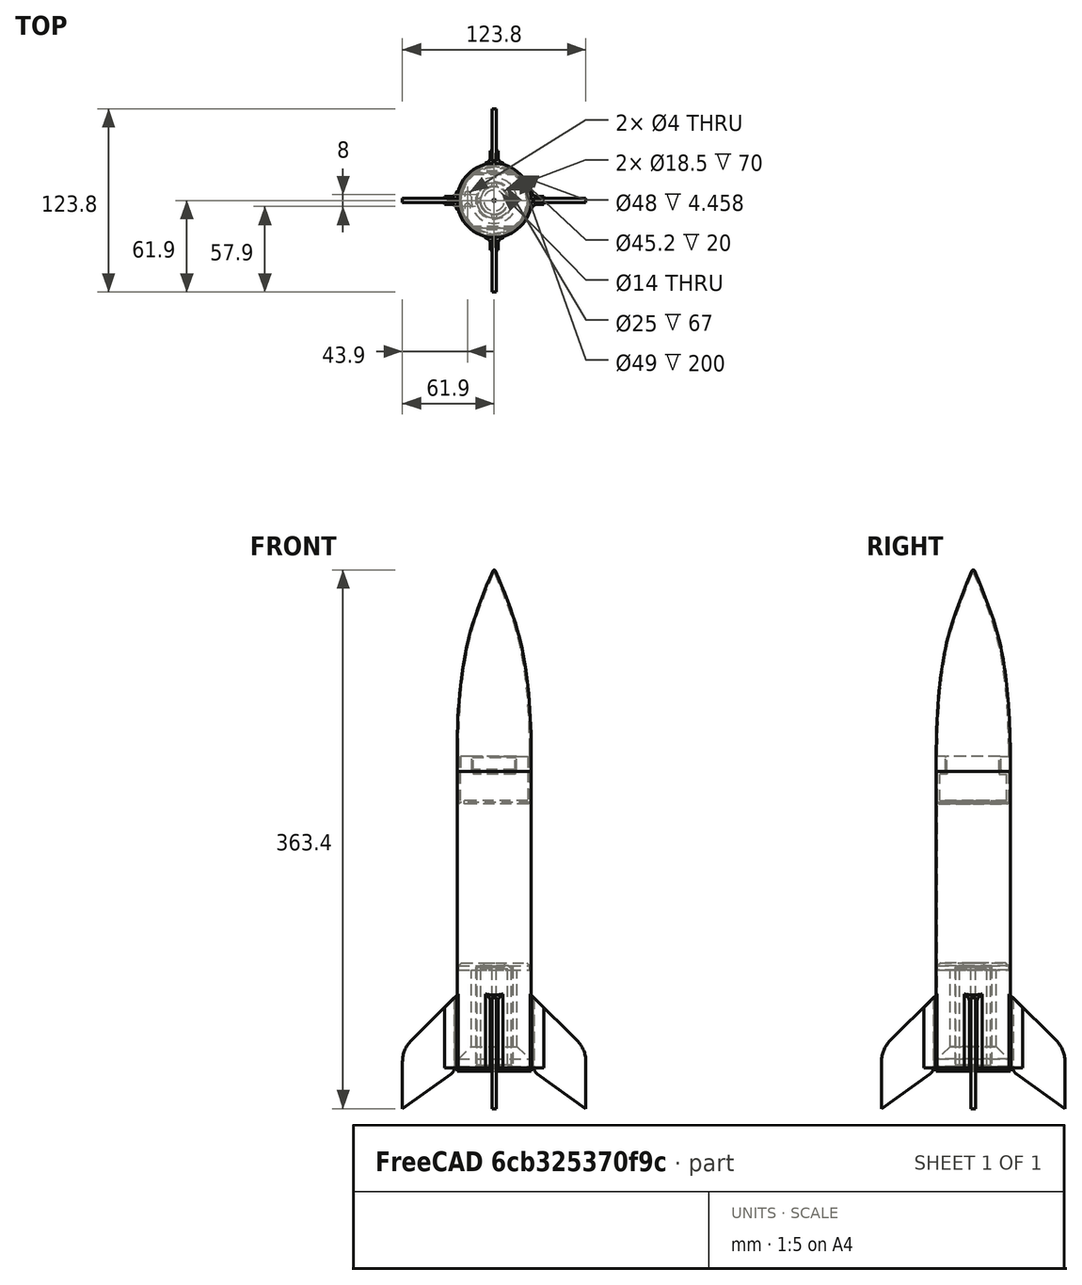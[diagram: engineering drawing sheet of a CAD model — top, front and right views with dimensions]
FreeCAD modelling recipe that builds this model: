
FCSTD DOCUMENT  (FreeCAD 0.19R)
Label: LaMule_support_moteur_V1
License: All rights reserved
LicenseURL: http://en.wikipedia.org/wiki/All_rights_reserved
objects: Sketcher::SketchObject×26, PartDesign::Pad×16, PartDesign::Body×14, PartDesign::Fillet×12, PartDesign::Pocket×8, PartDesign::Chamfer×7, Mesh::Feature×3, PartDesign::Revolution×2, App::LinkGroup×2, PartDesign::Thickness×1, TechDraw::DrawSVGTemplate×1, TechDraw::DrawViewPart×1, TechDraw::DrawPage×1
note: 132 computed .brp shape members not serialized (recipe doc carries the construction recipe); baked Part::Feature solids carry a one-line shape summary decoded from their .brp

FEATURE [Sketcher::SketchObject] Sketch
  FullyConstrained = true
  MapMode = 5
  Placement = pos=(0,0,0) rot=(1,0,0;1.5708rad)
  Support = -> [XZ_Plane]
  sketch-geometry (12):
    g0: LineSegment StartX=24 StartY=0 StartZ=0 EndX=7 EndY=0 EndZ=0
    g1: LineSegment StartX=7 StartY=0 StartZ=0 EndX=7 EndY=3 EndZ=0
    g2: LineSegment StartX=7 StartY=3 StartZ=0 EndX=12.5 EndY=3 EndZ=0
    g3: LineSegment StartX=12.5 StartY=3 StartZ=0 EndX=12.5 EndY=73 EndZ=0
    g4: LineSegment StartX=12.5 StartY=73 StartZ=0 EndX=25 EndY=73 EndZ=0
    g5: LineSegment StartX=25 StartY=73 StartZ=0 EndX=25 EndY=71 EndZ=0
    g6: LineSegment StartX=25 StartY=71 StartZ=0 EndX=24 EndY=70 EndZ=0
    g7: LineSegment StartX=24 StartY=70 StartZ=0 EndX=24 EndY=65 EndZ=0
    g8: LineSegment StartX=24 StartY=65 StartZ=0 EndX=15.5 EndY=56.5 EndZ=0
    g9: LineSegment StartX=15.5 StartY=56.5 StartZ=0 EndX=15.5 EndY=5 EndZ=0
    g10: LineSegment StartX=15.5 StartY=5 StartZ=0 EndX=24 EndY=5 EndZ=0
    g11: LineSegment StartX=24 StartY=5 StartZ=0 EndX=24 EndY=0 EndZ=0
  constraints (36):
    c: PointOnObject(g0,g-1)
    c: PointOnObject(g0,g-1)
    c: Coincident(g0,g1)
    c: Vertical(g1)
    c: Coincident(g1,g2)
    c: Horizontal(g2)
    c: Coincident(g2,g3)
    c: Vertical(g3)
    c: Coincident(g3,g4)
    c: Horizontal(g4)
    c: Coincident(g4,g5)
    c: Coincident(g5,g6)
    c: Coincident(g6,g7)
    c: Vertical(g7)
    c: Coincident(g7,g8)
    c: Coincident(g8,g9)
    c: Vertical(g9)
    c: Coincident(g9,g10)
    c: Horizontal(g10)
    c: Coincident(g10,g11)
    c: Coincident(g11,g0)
    c: DistanceX(g-2,g2) = 12.5
    c: DistanceY(g3,g3) = 70
    c: DistanceY(g1,g1) = 3
    c: DistanceX(g-2,g4) = 25
    c: Vertical(g5)
    c: DistanceY(g5,g5) = 2
    c: DistanceY(g7,g7) = 5
    c: DistanceX(g-1,g0) = 24
    c: DistanceX(g-2,g7) = 24
    c: Distance(g9,g3) = 3
    c: DistanceY(g11,g11) = 5
    c: Angle(g9,g8) = 2.35619
    c: Angle(g7,g6) = 2.35619
    c: Vertical(g11)
    c: DistanceX(g-2,g0) = 7
FEATURE [PartDesign::Revolution] Revolution
  Angle = 360
  Axis = (0,2e-16,1)
  Base = (0,0,0)
  Placement = pos=(0,0,0) rot=(1,0,0;1.5708rad)
  Profile = -> Sketch
  ReferenceAxis = -> Sketch [V_Axis]
  Reversed = true
FEATURE [PartDesign::Chamfer] Chamfer
  Angle = 45
  Base = -> Revolution [Edge6]
  BaseFeature = -> Revolution
  ChamferType = 0
  FlipDirection = false
  Placement = pos=(0,0,0) rot=(1,0,0;1.5708rad)
  Size = 3
  Size2 = 1
  SupportTransform = false
FEATURE [PartDesign::Chamfer] Chamfer001
  Angle = 45
  Base = -> Chamfer [Edge12]
  BaseFeature = -> Chamfer
  ChamferType = 0
  FlipDirection = false
  Placement = pos=(0,0,0) rot=(1,0,0;1.5708rad)
  Size = 2
  Size2 = 1
  SupportTransform = false
FEATURE [PartDesign::Body] Body  label="support_moteur_V1"
  Group = -> [Sketch,Revolution,Chamfer,Chamfer001]
  Origin = -> Origin
  Placement = pos=(7e-15,0,71) rot=(0,1,0;3.14159rad)
  Tip = -> Chamfer001
FEATURE [Sketcher::SketchObject] Sketch001
  FullyConstrained = true
  MapMode = 5
  Support = -> [XY_Plane001]
  sketch-geometry (2):
    g0: Circle CenterX=0 CenterY=0 CenterZ=0 NormalX=0 NormalY=0 NormalZ=1 AngleXU=0 Radius=24.5
    g1: Circle CenterX=0 CenterY=0 CenterZ=0 NormalX=0 NormalY=0 NormalZ=1 AngleXU=0 Radius=25
  constraints (4):
    c: Radius(g0) = 24.5
    c: Radius(g1) = 25
    c: Coincident(g0,g-1)
    c: Coincident(g1,g0)
FEATURE [PartDesign::Pad] Pad
  Direction = (1,1,1)
  Length = 200
  Length2 = 100
  Profile = -> Sketch001
  Type = 0
FEATURE [PartDesign::Body] Body001  label="tube_V1"
  Group = -> [Sketch001,Pad]
  Origin = -> Origin001
  Tip = -> Pad
FEATURE [Sketcher::SketchObject] Sketch002
  FullyConstrained = true
  MapMode = 5
  Support = -> [XY_Plane002]
  sketch-geometry (12):
    g0: ArcOfCircle CenterX=0 CenterY=0 CenterZ=0 NormalX=0 NormalY=0 NormalZ=1 AngleXU=0 Radius=25 StartAngle=6.04082 EndAngle=6.52555
    g1: LineSegment StartX=24.2693 StartY=-6 StartZ=0 EndX=25.2982 EndY=-6 EndZ=0
    g2: LineSegment StartX=24.2693 StartY=6 StartZ=0 EndX=25.2982 EndY=6 EndZ=0
    g3: LineSegment StartX=25.8697 StartY=2.6 StartZ=0 EndX=33.4517 EndY=2.6 EndZ=0
    g4: LineSegment StartX=33.4517 StartY=2.6 StartZ=0 EndX=33.4517 EndY=1.6 EndZ=0
    g5: LineSegment StartX=33.4517 StartY=1.6 StartZ=0 EndX=26.4517 EndY=1.6 EndZ=0
    g6: LineSegment StartX=26.4517 StartY=1.6 StartZ=0 EndX=26.4517 EndY=-1.6 EndZ=0
    g7: LineSegment StartX=26.4517 StartY=-1.6 StartZ=0 EndX=33.4517 EndY=-1.6 EndZ=0
    g8: LineSegment StartX=33.4517 StartY=-1.6 StartZ=0 EndX=33.4517 EndY=-2.6 EndZ=0
    g9: LineSegment StartX=33.4517 StartY=-2.6 StartZ=0 EndX=25.8697 EndY=-2.6 EndZ=0
    g10: ArcOfCircle CenterX=0 CenterY=0 CenterZ=0 NormalX=0 NormalY=0 NormalZ=1 AngleXU=0 Radius=26 StartAngle=6.05032 EndAngle=6.18302
    g11: ArcOfCircle CenterX=0 CenterY=0 CenterZ=0 NormalX=0 NormalY=0 NormalZ=1 AngleXU=0 Radius=26 StartAngle=0.100167 EndAngle=0.232868
  constraints (33):
    c: Coincident(g0,g-1)
    c: Radius(g0) = 25
    c: Coincident(g0,g1)
    c: Coincident(g0,g2)
    c: Horizontal(g3)
    c: Coincident(g3,g4)
    c: Coincident(g4,g5)
    c: Horizontal(g5)
    c: Coincident(g5,g6)
    c: Coincident(g6,g7)
    c: Horizontal(g7)
    c: Coincident(g7,g8)
    c: Coincident(g8,g9)
    c: Horizontal(g9)
    c: Coincident(g10,g0)
    c: Coincident(g10,g1)
    c: Coincident(g10,g9)
    c: Coincident(g11,g0)
    c: Coincident(g11,g2)
    c: Coincident(g11,g3)
    c: Radius(g11) = 26
    c: Horizontal(g2)
    c: Horizontal(g1)
    c: Symmetric(g7,g4,g-1)
    c: Vertical(g8)
    c: Vertical(g6)
    c: Distance(g6,g5) = 3.2
    c: DistanceY(g4,g4) = 1
    c: Distance(g5,g0) = 26.5
    c: Symmetric(g3,g8,g-1)
    c: DistanceX(g5,g5) = 7
    c: Symmetric(g2,g1,g-1)
    c: DistanceY(g-1,g2) = 6
FEATURE [PartDesign::Pad] Pad001
  Direction = (1,1,1)
  Length = 50
  Length2 = 100
  Profile = -> Sketch002
  Type = 0
FEATURE [PartDesign::Fillet] Fillet
  Base = -> Pad001 [Edge20,Edge1]
  BaseFeature = -> Pad001
  Radius = 4
  SupportTransform = false
FEATURE [Sketcher::SketchObject] Sketch003
  ExternalGeometry = -> [Fillet]
  FullyConstrained = true
  MapMode = 5
  Placement = pos=(0,-2.6,0) rot=(1,0,0;1.5708rad)
  Support = -> [Fillet]
  sketch-geometry (3):
    g0: LineSegment StartX=33.4517 StartY=50 StartZ=0 EndX=33.4517 EndY=40.8177 EndZ=0
    g1: LineSegment StartX=33.4517 StartY=40.8177 StartZ=0 EndX=24.2693 EndY=50 EndZ=0
    g2: LineSegment StartX=24.2693 StartY=50 StartZ=0 EndX=33.4517 EndY=50 EndZ=0
  constraints (8):
    c: Coincident(g-4,g0)
    c: PointOnObject(g0,g-4)
    c: Coincident(g0,g1)
    c: PointOnObject(g1,g-3)
    c: Coincident(g1,g2)
    c: Coincident(g2,g0)
    c: Horizontal(g2)
    c: Angle(g1,g2) = 0.785398
FEATURE [PartDesign::Pocket] Pocket
  BaseFeature = -> Fillet
  Length = 23
  Length2 = 100
  Midplane = true
  Profile = -> Sketch003
  Type = 1
FEATURE [PartDesign::Body] Body002  label="support_aileron_V1"
  Group = -> [Sketch002,Pad001,Fillet,Sketch003,Pocket]
  Origin = -> Origin002
  Tip = -> Pocket
FEATURE [Sketcher::SketchObject] Sketch004
  FullyConstrained = true
  MapMode = 5
  Support = -> [XY_Plane003]
  sketch-geometry (12):
    g0: ArcOfCircle CenterX=0 CenterY=0 CenterZ=0 NormalX=0 NormalY=0 NormalZ=1 AngleXU=0 Radius=25 StartAngle=6.04082 EndAngle=6.52555
    g1: LineSegment StartX=24.2693 StartY=-6 StartZ=0 EndX=25.2982 EndY=-6 EndZ=0
    g2: LineSegment StartX=24.2693 StartY=6 StartZ=0 EndX=25.2982 EndY=6 EndZ=0
    g3: LineSegment StartX=25.8697 StartY=2.6 StartZ=0 EndX=33.4517 EndY=2.6 EndZ=0
    g4: LineSegment StartX=33.4517 StartY=2.6 StartZ=0 EndX=33.4517 EndY=1.6 EndZ=0
    g5: LineSegment StartX=33.4517 StartY=1.6 StartZ=0 EndX=26.4517 EndY=1.6 EndZ=0
    g6: LineSegment StartX=26.4517 StartY=1.6 StartZ=0 EndX=26.4517 EndY=-1.6 EndZ=0
    g7: LineSegment StartX=26.4517 StartY=-1.6 StartZ=0 EndX=33.4517 EndY=-1.6 EndZ=0
    g8: LineSegment StartX=33.4517 StartY=-1.6 StartZ=0 EndX=33.4517 EndY=-2.6 EndZ=0
    g9: LineSegment StartX=33.4517 StartY=-2.6 StartZ=0 EndX=25.8697 EndY=-2.6 EndZ=0
    g10: ArcOfCircle CenterX=0 CenterY=0 CenterZ=0 NormalX=0 NormalY=0 NormalZ=1 AngleXU=0 Radius=26 StartAngle=6.05032 EndAngle=6.18302
    g11: ArcOfCircle CenterX=0 CenterY=0 CenterZ=0 NormalX=0 NormalY=0 NormalZ=1 AngleXU=0 Radius=26 StartAngle=0.100167 EndAngle=0.232868
  constraints (33):
    c: Coincident(g0,g-1)
    c: Radius(g0) = 25
    c: Coincident(g0,g1)
    c: Coincident(g0,g2)
    c: Horizontal(g3)
    c: Coincident(g3,g4)
    c: Coincident(g4,g5)
    c: Horizontal(g5)
    c: Coincident(g5,g6)
    c: Coincident(g6,g7)
    c: Horizontal(g7)
    c: Coincident(g7,g8)
    c: Coincident(g8,g9)
    c: Horizontal(g9)
    c: Coincident(g10,g0)
    c: Coincident(g10,g1)
    c: Coincident(g10,g9)
    c: Coincident(g11,g0)
    c: Coincident(g11,g2)
    c: Coincident(g11,g3)
    c: Radius(g11) = 26
    c: Horizontal(g2)
    c: Horizontal(g1)
    c: Symmetric(g7,g4,g-1)
    c: Vertical(g8)
    c: Vertical(g6)
    c: Distance(g6,g5) = 3.2
    c: DistanceY(g4,g4) = 1
    c: Distance(g5,g0) = 26.5
    c: Symmetric(g3,g8,g-1)
    c: DistanceX(g5,g5) = 7
    c: Symmetric(g2,g1,g-1)
    c: DistanceY(g-1,g2) = 6
FEATURE [PartDesign::Pad] Pad002
  Direction = (1,1,1)
  Length = 50
  Length2 = 100
  Profile = -> Sketch004
  Type = 0
FEATURE [PartDesign::Fillet] Fillet001
  Base = -> Pad002 [Edge20,Edge1]
  BaseFeature = -> Pad002
  Radius = 4
  SupportTransform = false
FEATURE [Sketcher::SketchObject] Sketch005
  ExternalGeometry = -> [Fillet001]
  FullyConstrained = true
  MapMode = 5
  Placement = pos=(0,-2.6,0) rot=(1,0,0;1.5708rad)
  Support = -> [Fillet001]
  sketch-geometry (3):
    g0: LineSegment StartX=33.4517 StartY=50 StartZ=0 EndX=33.4517 EndY=40.8177 EndZ=0
    g1: LineSegment StartX=33.4517 StartY=40.8177 StartZ=0 EndX=24.2693 EndY=50 EndZ=0
    g2: LineSegment StartX=24.2693 StartY=50 StartZ=0 EndX=33.4517 EndY=50 EndZ=0
  constraints (8):
    c: Coincident(g-4,g0)
    c: PointOnObject(g0,g-4)
    c: Coincident(g0,g1)
    c: PointOnObject(g1,g-3)
    c: Coincident(g1,g2)
    c: Coincident(g2,g0)
    c: Horizontal(g2)
    c: Angle(g1,g2) = 0.785398
FEATURE [PartDesign::Pocket] Pocket001
  BaseFeature = -> Fillet001
  Length = 23
  Length2 = 100
  Midplane = true
  Profile = -> Sketch005
  Type = 1
FEATURE [PartDesign::Body] Body003  label="support_aileron_V002"
  Group = -> [Sketch004,Pad002,Fillet001,Sketch005,Pocket001]
  Origin = -> Origin003
  Placement = pos=(0,0,0) rot=(0,0,1;1.5708rad)
  Tip = -> Pocket001
FEATURE [Sketcher::SketchObject] Sketch006
  FullyConstrained = true
  MapMode = 5
  Support = -> [XY_Plane004]
  sketch-geometry (12):
    g0: ArcOfCircle CenterX=0 CenterY=0 CenterZ=0 NormalX=0 NormalY=0 NormalZ=1 AngleXU=0 Radius=25 StartAngle=6.04082 EndAngle=6.52555
    g1: LineSegment StartX=24.2693 StartY=-6 StartZ=0 EndX=25.2982 EndY=-6 EndZ=0
    g2: LineSegment StartX=24.2693 StartY=6 StartZ=0 EndX=25.2982 EndY=6 EndZ=0
    g3: LineSegment StartX=25.8697 StartY=2.6 StartZ=0 EndX=33.4517 EndY=2.6 EndZ=0
    g4: LineSegment StartX=33.4517 StartY=2.6 StartZ=0 EndX=33.4517 EndY=1.6 EndZ=0
    g5: LineSegment StartX=33.4517 StartY=1.6 StartZ=0 EndX=26.4517 EndY=1.6 EndZ=0
    g6: LineSegment StartX=26.4517 StartY=1.6 StartZ=0 EndX=26.4517 EndY=-1.6 EndZ=0
    g7: LineSegment StartX=26.4517 StartY=-1.6 StartZ=0 EndX=33.4517 EndY=-1.6 EndZ=0
    g8: LineSegment StartX=33.4517 StartY=-1.6 StartZ=0 EndX=33.4517 EndY=-2.6 EndZ=0
    g9: LineSegment StartX=33.4517 StartY=-2.6 StartZ=0 EndX=25.8697 EndY=-2.6 EndZ=0
    g10: ArcOfCircle CenterX=0 CenterY=0 CenterZ=0 NormalX=0 NormalY=0 NormalZ=1 AngleXU=0 Radius=26 StartAngle=6.05032 EndAngle=6.18302
    g11: ArcOfCircle CenterX=0 CenterY=0 CenterZ=0 NormalX=0 NormalY=0 NormalZ=1 AngleXU=0 Radius=26 StartAngle=0.100167 EndAngle=0.232868
  constraints (33):
    c: Coincident(g0,g-1)
    c: Radius(g0) = 25
    c: Coincident(g0,g1)
    c: Coincident(g0,g2)
    c: Horizontal(g3)
    c: Coincident(g3,g4)
    c: Coincident(g4,g5)
    c: Horizontal(g5)
    c: Coincident(g5,g6)
    c: Coincident(g6,g7)
    c: Horizontal(g7)
    c: Coincident(g7,g8)
    c: Coincident(g8,g9)
    c: Horizontal(g9)
    c: Coincident(g10,g0)
    c: Coincident(g10,g1)
    c: Coincident(g10,g9)
    c: Coincident(g11,g0)
    c: Coincident(g11,g2)
    c: Coincident(g11,g3)
    c: Radius(g11) = 26
    c: Horizontal(g2)
    c: Horizontal(g1)
    c: Symmetric(g7,g4,g-1)
    c: Vertical(g8)
    c: Vertical(g6)
    c: Distance(g6,g5) = 3.2
    c: DistanceY(g4,g4) = 1
    c: Distance(g5,g0) = 26.5
    c: Symmetric(g3,g8,g-1)
    c: DistanceX(g5,g5) = 7
    c: Symmetric(g2,g1,g-1)
    c: DistanceY(g-1,g2) = 6
FEATURE [PartDesign::Pad] Pad003
  Direction = (1,1,1)
  Length = 50
  Length2 = 100
  Profile = -> Sketch006
  Type = 0
FEATURE [PartDesign::Fillet] Fillet002
  Base = -> Pad003 [Edge20,Edge1]
  BaseFeature = -> Pad003
  Radius = 4
  SupportTransform = false
FEATURE [Sketcher::SketchObject] Sketch007
  ExternalGeometry = -> [Fillet002]
  FullyConstrained = true
  MapMode = 5
  Placement = pos=(0,-2.6,0) rot=(1,0,0;1.5708rad)
  Support = -> [Fillet002]
  sketch-geometry (3):
    g0: LineSegment StartX=33.4517 StartY=50 StartZ=0 EndX=33.4517 EndY=40.8177 EndZ=0
    g1: LineSegment StartX=33.4517 StartY=40.8177 StartZ=0 EndX=24.2693 EndY=50 EndZ=0
    g2: LineSegment StartX=24.2693 StartY=50 StartZ=0 EndX=33.4517 EndY=50 EndZ=0
  constraints (8):
    c: Coincident(g-4,g0)
    c: PointOnObject(g0,g-4)
    c: Coincident(g0,g1)
    c: PointOnObject(g1,g-3)
    c: Coincident(g1,g2)
    c: Coincident(g2,g0)
    c: Horizontal(g2)
    c: Angle(g1,g2) = 0.785398
FEATURE [PartDesign::Pocket] Pocket002
  BaseFeature = -> Fillet002
  Length = 23
  Length2 = 100
  Midplane = true
  Profile = -> Sketch007
  Type = 1
FEATURE [PartDesign::Body] Body004  label="support_aileron_V003"
  Group = -> [Sketch006,Pad003,Fillet002,Sketch007,Pocket002]
  Origin = -> Origin004
  Placement = pos=(0,0,0) rot=(0,0,1;3.14159rad)
  Tip = -> Pocket002
FEATURE [Sketcher::SketchObject] Sketch008
  FullyConstrained = true
  MapMode = 5
  Support = -> [XY_Plane005]
  sketch-geometry (12):
    g0: ArcOfCircle CenterX=0 CenterY=0 CenterZ=0 NormalX=0 NormalY=0 NormalZ=1 AngleXU=0 Radius=25 StartAngle=6.04082 EndAngle=6.52555
    g1: LineSegment StartX=24.2693 StartY=-6 StartZ=0 EndX=25.2982 EndY=-6 EndZ=0
    g2: LineSegment StartX=24.2693 StartY=6 StartZ=0 EndX=25.2982 EndY=6 EndZ=0
    g3: LineSegment StartX=25.8697 StartY=2.6 StartZ=0 EndX=33.4517 EndY=2.6 EndZ=0
    g4: LineSegment StartX=33.4517 StartY=2.6 StartZ=0 EndX=33.4517 EndY=1.6 EndZ=0
    g5: LineSegment StartX=33.4517 StartY=1.6 StartZ=0 EndX=26.4517 EndY=1.6 EndZ=0
    g6: LineSegment StartX=26.4517 StartY=1.6 StartZ=0 EndX=26.4517 EndY=-1.6 EndZ=0
    g7: LineSegment StartX=26.4517 StartY=-1.6 StartZ=0 EndX=33.4517 EndY=-1.6 EndZ=0
    g8: LineSegment StartX=33.4517 StartY=-1.6 StartZ=0 EndX=33.4517 EndY=-2.6 EndZ=0
    g9: LineSegment StartX=33.4517 StartY=-2.6 StartZ=0 EndX=25.8697 EndY=-2.6 EndZ=0
    g10: ArcOfCircle CenterX=0 CenterY=0 CenterZ=0 NormalX=0 NormalY=0 NormalZ=1 AngleXU=0 Radius=26 StartAngle=6.05032 EndAngle=6.18302
    g11: ArcOfCircle CenterX=0 CenterY=0 CenterZ=0 NormalX=0 NormalY=0 NormalZ=1 AngleXU=0 Radius=26 StartAngle=0.100167 EndAngle=0.232868
  constraints (33):
    c: Coincident(g0,g-1)
    c: Radius(g0) = 25
    c: Coincident(g0,g1)
    c: Coincident(g0,g2)
    c: Horizontal(g3)
    c: Coincident(g3,g4)
    c: Coincident(g4,g5)
    c: Horizontal(g5)
    c: Coincident(g5,g6)
    c: Coincident(g6,g7)
    c: Horizontal(g7)
    c: Coincident(g7,g8)
    c: Coincident(g8,g9)
    c: Horizontal(g9)
    c: Coincident(g10,g0)
    c: Coincident(g10,g1)
    c: Coincident(g10,g9)
    c: Coincident(g11,g0)
    c: Coincident(g11,g2)
    c: Coincident(g11,g3)
    c: Radius(g11) = 26
    c: Horizontal(g2)
    c: Horizontal(g1)
    c: Symmetric(g7,g4,g-1)
    c: Vertical(g8)
    c: Vertical(g6)
    c: Distance(g6,g5) = 3.2
    c: DistanceY(g4,g4) = 1
    c: Distance(g5,g0) = 26.5
    c: Symmetric(g3,g8,g-1)
    c: DistanceX(g5,g5) = 7
    c: Symmetric(g2,g1,g-1)
    c: DistanceY(g-1,g2) = 6
FEATURE [PartDesign::Pad] Pad004
  Direction = (1,1,1)
  Length = 50
  Length2 = 100
  Profile = -> Sketch008
  Type = 0
FEATURE [PartDesign::Fillet] Fillet003
  Base = -> Pad004 [Edge20,Edge1]
  BaseFeature = -> Pad004
  Radius = 4
  SupportTransform = false
FEATURE [Sketcher::SketchObject] Sketch009
  ExternalGeometry = -> [Fillet003]
  FullyConstrained = true
  MapMode = 5
  Placement = pos=(0,-2.6,0) rot=(1,0,0;1.5708rad)
  Support = -> [Fillet003]
  sketch-geometry (3):
    g0: LineSegment StartX=33.4517 StartY=50 StartZ=0 EndX=33.4517 EndY=40.8177 EndZ=0
    g1: LineSegment StartX=33.4517 StartY=40.8177 StartZ=0 EndX=24.2693 EndY=50 EndZ=0
    g2: LineSegment StartX=24.2693 StartY=50 StartZ=0 EndX=33.4517 EndY=50 EndZ=0
  constraints (8):
    c: Coincident(g-4,g0)
    c: PointOnObject(g0,g-4)
    c: Coincident(g0,g1)
    c: PointOnObject(g1,g-3)
    c: Coincident(g1,g2)
    c: Coincident(g2,g0)
    c: Horizontal(g2)
    c: Angle(g1,g2) = 0.785398
FEATURE [PartDesign::Pocket] Pocket003
  BaseFeature = -> Fillet003
  Length = 23
  Length2 = 100
  Midplane = true
  Profile = -> Sketch009
  Type = 1
FEATURE [PartDesign::Body] Body005  label="support_aileron_V004"
  Group = -> [Sketch008,Pad004,Fillet003,Sketch009,Pocket003]
  Origin = -> Origin005
  Placement = pos=(0,0,0) rot=(0,0,-1;1.5708rad)
  Tip = -> Pocket003
FEATURE [App::LinkGroup] LinkGroup  label="support_ailerons_V1"
  ElementList = -> [Body005,Body004,Body003,Body002]
  LinkMode = 0
FEATURE [Sketcher::SketchObject] Sketch010
  FullyConstrained = true
  MapMode = 5
  Placement = pos=(0,0,0) rot=(0.57735,0.57735,0.57735;2.0944rad)
  Support = -> [YZ_Plane006]
  sketch-geometry (4):
    g0: LineSegment StartX=27 StartY=-2.5 StartZ=0 EndX=61.9 EndY=-27.4 EndZ=0
    g1: LineSegment StartX=61.9 StartY=-27.4 StartZ=0 EndX=61.9 EndY=12.6 EndZ=0
    g2: LineSegment StartX=61.9 StartY=12.6 StartZ=0 EndX=27 EndY=47.5 EndZ=0
    g3: LineSegment StartX=27 StartY=47.5 StartZ=0 EndX=27 EndY=-2.5 EndZ=0
  constraints (12):
    c: Coincident(g0,g1)
    c: Vertical(g1)
    c: Coincident(g1,g2)
    c: Coincident(g2,g3)
    c: Coincident(g3,g0)
    c: Vertical(g3)
    c: DistanceY(g3,g3) = 50
    c: DistanceY(g-1,g2) = 47.5
    c: DistanceX(g-2,g0) = 27
    c: Angle(g3,g2) = 0.785398
    c: DistanceY(g1,g1) = 40
    c: DistanceX(g-2,g0) = 61.9
FEATURE [PartDesign::Pad] Pad005
  Direction = (1,1,1)
  Length = 3
  Length2 = 100
  Midplane = true
  Placement = pos=(0,0,0) rot=(0.57735,0.57735,0.57735;2.0944rad)
  Profile = -> Sketch010
  Type = 0
FEATURE [PartDesign::Fillet] Fillet004
  Base = -> Pad005 [Edge5]
  BaseFeature = -> Pad005
  Placement = pos=(0,0,0) rot=(0.57735,0.57735,0.57735;2.0944rad)
  Radius = 20
  SupportTransform = false
FEATURE [PartDesign::Fillet] Fillet005
  Base = -> Fillet004 [Edge11]
  BaseFeature = -> Fillet004
  Placement = pos=(0,0,0) rot=(0.57735,0.57735,0.57735;2.0944rad)
  Radius = 5
  SupportTransform = false
FEATURE [PartDesign::Body] Body006  label="ailerons_V1"
  Group = -> [Sketch010,Pad005,Fillet004,Fillet005]
  Origin = -> Origin006
  Tip = -> Fillet005
FEATURE [Sketcher::SketchObject] Sketch011
  FullyConstrained = true
  MapMode = 5
  Placement = pos=(0,0,0) rot=(0.57735,0.57735,0.57735;2.0944rad)
  Support = -> [YZ_Plane007]
  sketch-geometry (4):
    g0: LineSegment StartX=27 StartY=-2.5 StartZ=0 EndX=61.9 EndY=-27.4 EndZ=0
    g1: LineSegment StartX=61.9 StartY=-27.4 StartZ=0 EndX=61.9 EndY=12.6 EndZ=0
    g2: LineSegment StartX=61.9 StartY=12.6 StartZ=0 EndX=27 EndY=47.5 EndZ=0
    g3: LineSegment StartX=27 StartY=47.5 StartZ=0 EndX=27 EndY=-2.5 EndZ=0
  constraints (12):
    c: Coincident(g0,g1)
    c: Vertical(g1)
    c: Coincident(g1,g2)
    c: Coincident(g2,g3)
    c: Coincident(g3,g0)
    c: Vertical(g3)
    c: DistanceY(g3,g3) = 50
    c: DistanceY(g-1,g2) = 47.5
    c: DistanceX(g-2,g0) = 27
    c: Angle(g3,g2) = 0.785398
    c: DistanceY(g1,g1) = 40
    c: DistanceX(g-2,g0) = 61.9
FEATURE [PartDesign::Pad] Pad006
  Direction = (1,1,1)
  Length = 3
  Length2 = 100
  Midplane = true
  Placement = pos=(0,0,0) rot=(0.57735,0.57735,0.57735;2.0944rad)
  Profile = -> Sketch011
  Type = 0
FEATURE [PartDesign::Fillet] Fillet006
  Base = -> Pad006 [Edge5]
  BaseFeature = -> Pad006
  Placement = pos=(0,0,0) rot=(0.57735,0.57735,0.57735;2.0944rad)
  Radius = 20
  SupportTransform = false
FEATURE [PartDesign::Fillet] Fillet007
  Base = -> Fillet006 [Edge11]
  BaseFeature = -> Fillet006
  Placement = pos=(0,0,0) rot=(0.57735,0.57735,0.57735;2.0944rad)
  Radius = 5
  SupportTransform = false
FEATURE [PartDesign::Body] Body007  label="ailerons_V002"
  Group = -> [Sketch011,Pad006,Fillet006,Fillet007]
  Origin = -> Origin007
  Placement = pos=(0,0,0) rot=(0,0,1;3.14159rad)
  Tip = -> Fillet007
FEATURE [Sketcher::SketchObject] Sketch012
  FullyConstrained = true
  MapMode = 5
  Placement = pos=(0,0,0) rot=(0.57735,0.57735,0.57735;2.0944rad)
  Support = -> [YZ_Plane008]
  sketch-geometry (4):
    g0: LineSegment StartX=27 StartY=-2.5 StartZ=0 EndX=61.9 EndY=-27.4 EndZ=0
    g1: LineSegment StartX=61.9 StartY=-27.4 StartZ=0 EndX=61.9 EndY=12.6 EndZ=0
    g2: LineSegment StartX=61.9 StartY=12.6 StartZ=0 EndX=27 EndY=47.5 EndZ=0
    g3: LineSegment StartX=27 StartY=47.5 StartZ=0 EndX=27 EndY=-2.5 EndZ=0
  constraints (12):
    c: Coincident(g0,g1)
    c: Vertical(g1)
    c: Coincident(g1,g2)
    c: Coincident(g2,g3)
    c: Coincident(g3,g0)
    c: Vertical(g3)
    c: DistanceY(g3,g3) = 50
    c: DistanceY(g-1,g2) = 47.5
    c: DistanceX(g-2,g0) = 27
    c: Angle(g3,g2) = 0.785398
    c: DistanceY(g1,g1) = 40
    c: DistanceX(g-2,g0) = 61.9
FEATURE [PartDesign::Pad] Pad007
  Direction = (1,1,1)
  Length = 3
  Length2 = 100
  Midplane = true
  Placement = pos=(0,0,0) rot=(0.57735,0.57735,0.57735;2.0944rad)
  Profile = -> Sketch012
  Type = 0
FEATURE [PartDesign::Fillet] Fillet008
  Base = -> Pad007 [Edge5]
  BaseFeature = -> Pad007
  Placement = pos=(0,0,0) rot=(0.57735,0.57735,0.57735;2.0944rad)
  Radius = 20
  SupportTransform = false
FEATURE [PartDesign::Fillet] Fillet009
  Base = -> Fillet008 [Edge11]
  BaseFeature = -> Fillet008
  Placement = pos=(0,0,0) rot=(0.57735,0.57735,0.57735;2.0944rad)
  Radius = 5
  SupportTransform = false
FEATURE [PartDesign::Body] Body008  label="ailerons_V003"
  Group = -> [Sketch012,Pad007,Fillet008,Fillet009]
  Origin = -> Origin008
  Placement = pos=(0,0,0) rot=(0,0,1;1.5708rad)
  Tip = -> Fillet009
FEATURE [Sketcher::SketchObject] Sketch013
  FullyConstrained = true
  MapMode = 5
  Placement = pos=(0,0,0) rot=(0.57735,0.57735,0.57735;2.0944rad)
  Support = -> [YZ_Plane009]
  sketch-geometry (4):
    g0: LineSegment StartX=27 StartY=-2.5 StartZ=0 EndX=61.9 EndY=-27.4 EndZ=0
    g1: LineSegment StartX=61.9 StartY=-27.4 StartZ=0 EndX=61.9 EndY=12.6 EndZ=0
    g2: LineSegment StartX=61.9 StartY=12.6 StartZ=0 EndX=27 EndY=47.5 EndZ=0
    g3: LineSegment StartX=27 StartY=47.5 StartZ=0 EndX=27 EndY=-2.5 EndZ=0
  constraints (12):
    c: Coincident(g0,g1)
    c: Vertical(g1)
    c: Coincident(g1,g2)
    c: Coincident(g2,g3)
    c: Coincident(g3,g0)
    c: Vertical(g3)
    c: DistanceY(g3,g3) = 50
    c: DistanceY(g-1,g2) = 47.5
    c: DistanceX(g-2,g0) = 27
    c: Angle(g3,g2) = 0.785398
    c: DistanceY(g1,g1) = 40
    c: DistanceX(g-2,g0) = 61.9
FEATURE [PartDesign::Pad] Pad008
  Direction = (1,1,1)
  Length = 3
  Length2 = 100
  Midplane = true
  Placement = pos=(0,0,0) rot=(0.57735,0.57735,0.57735;2.0944rad)
  Profile = -> Sketch013
  Type = 0
FEATURE [PartDesign::Fillet] Fillet010
  Base = -> Pad008 [Edge5]
  BaseFeature = -> Pad008
  Placement = pos=(0,0,0) rot=(0.57735,0.57735,0.57735;2.0944rad)
  Radius = 20
  SupportTransform = false
FEATURE [PartDesign::Fillet] Fillet011
  Base = -> Fillet010 [Edge11]
  BaseFeature = -> Fillet010
  Placement = pos=(0,0,0) rot=(0.57735,0.57735,0.57735;2.0944rad)
  Radius = 5
  SupportTransform = false
FEATURE [PartDesign::Body] Body009  label="ailerons_V004"
  Group = -> [Sketch013,Pad008,Fillet010,Fillet011]
  Origin = -> Origin009
  Placement = pos=(0,0,0) rot=(0,0,-1;1.5708rad)
  Tip = -> Fillet011
FEATURE [App::LinkGroup] LinkGroup001  label="ailerons"
  ElementList = -> [Body009,Body008,Body007,Body006]
  LinkMode = 0
FEATURE [Sketcher::SketchObject] Sketch014
  FullyConstrained = true
  MapMode = 5
  Support = -> [XY_Plane010]
  sketch-geometry (12):
    g0: LineSegment StartX=0 StartY=0 StartZ=0 EndX=134.73 EndY=0 EndZ=0
    g1: LineSegment StartX=134.73 StartY=-24 StartZ=0 EndX=134.73 EndY=0 EndZ=0
    g2: LineSegment StartX=134.73 StartY=-24 StartZ=0 EndX=120.272 EndY=-24 EndZ=0
    g3-g7: Circle x5 (B-spline internal-alignment scaffolding for g8; pole/knot coordinates omitted)
    g8: BSplineCurve PolesCount=5 KnotsCount=3 Degree=3 IsPeriodic=0
    g9: GeomPoint X=120.272 Y=-24 Z=0
    g10: GeomPoint X=62.1183 Y=-19.6849 Z=0
    g11: GeomPoint X=0 Y=0 Z=0
  constraints (23):
    c: Coincident(g0,g-1)
    c: PointOnObject(g0,g-1)
    c: Coincident(g1,g0)
    c: Vertical(g1)
    c: Coincident(g2,g1)
    c: Horizontal(g2)
    c: Coincident(g8,g2)
    c: Weight(g3) = 1
    c: Equal(g3, g4-g7) x4
    c: Coincident(g8,g0)
    c: InternalAlignment(g3-g7 -> g8) x5
    c: InternalAlignment(g9,g8)
    c: InternalAlignment(g10,g8)
    c: InternalAlignment(g11,g8)
    c: DistanceX(g6) = 33.4091
    c: DistanceY(g6) = -14.1378
    c: DistanceX(g5) = 61.0359
    c: DistanceY(g5) = -20.426
    c: DistanceX(g4) = 92.9923
    c: DistanceY(g4) = -23.75
    c: DistanceX(g2) = 120.272
    c: DistanceY(g2) = -24
    c: DistanceX(g0,g0) = 134.73
FEATURE [PartDesign::Revolution] Revolution001
  Angle = 360
  Axis = (1,0,0)
  Base = (0,0,0)
  Profile = -> Sketch014
  ReferenceAxis = -> X_Axis010
  Reversed = true
FEATURE [PartDesign::Thickness] Thickness
  Base = -> Revolution001 [Face1]
  BaseFeature = -> Revolution001
  Intersection = false
  Join = 0
  Mode = 0
  SupportTransform = false
  Value = 1
FEATURE [Sketcher::SketchObject] Sketch015
  FullyConstrained = true
  MapMode = 5
  Placement = pos=(134.73,0,0) rot=(0.57735,0.57735,0.57735;2.0944rad)
  Support = -> [Thickness]
  sketch-geometry (5):
    g0: Circle CenterX=1.1e-15 CenterY=0 CenterZ=0 NormalX=0 NormalY=0 NormalZ=1 AngleXU=0 Radius=25
    g1: ArcOfCircle CenterX=1.1e-15 CenterY=0 CenterZ=0 NormalX=0 NormalY=0 NormalZ=1 AngleXU=0 Radius=24 StartAngle=0.675132 EndAngle=2.46646
    g2: ArcOfCircle CenterX=1.1e-15 CenterY=0 CenterZ=0 NormalX=0 NormalY=0 NormalZ=1 AngleXU=0 Radius=24 StartAngle=3.81672 EndAngle=5.60805
    g3: LineSegment StartX=-18.735 StartY=15 StartZ=0 EndX=-18.735 EndY=-15 EndZ=0
    g4: LineSegment StartX=18.735 StartY=15 StartZ=0 EndX=18.735 EndY=-15 EndZ=0
  constraints (14):
    c: Coincident(g0,g-1)
    c: Radius(g0) = 25
    c: Coincident(g1,g0)
    c: Coincident(g2,g0)
    c: Symmetric(g2,g2,g-2)
    c: Symmetric(g2,g1,g-1)
    c: Radius(g1) = 24
    c: Equal(g1,g2)
    c: Coincident(g3,g1)
    c: Coincident(g3,g2)
    c: Coincident(g4,g1)
    c: Coincident(g4,g2)
    c: Symmetric(g1,g1,g-2)
    c: DistanceY(g4,g4) = 30
FEATURE [PartDesign::Pad] Pad009
  BaseFeature = -> Thickness
  Direction = (1,1,1)
  Length = 10
  Length2 = 100
  Profile = -> Sketch015
  Reversed = true
  Type = 0
FEATURE [PartDesign::Chamfer] Chamfer002
  Angle = 45
  Base = -> Pad009 [Edge9,Edge6]
  BaseFeature = -> Pad009
  ChamferType = 0
  FlipDirection = false
  Size = 1
  Size2 = 1
  SupportTransform = false
FEATURE [PartDesign::Body] Body010  label="coiffe_V1"
  Group = -> [Sketch014,Revolution001,Thickness,Sketch015,Pad009,Chamfer002]
  Origin = -> Origin010
  Placement = pos=(-7.4e-14,0,335) rot=(0,1,0;1.5708rad)
  Tip = -> Chamfer002
FEATURE [Mesh::Feature] Mesh  label="coiffe_V1 (Meshed)"
FEATURE [TechDraw::DrawSVGTemplate] Template
  EditableTexts = Approved1=N/A; Approved2=N/A; CheckedBy=Papas Inventeurs; Code=Code; CompanyAddress=planête Terre, système solaire; CompanyName=Lift Off; DrawingNumber=1; DrawingTitle1=LaMule; DrawingTitle2=Envoyons quelque chose en l'air!; DrawingTitle3="Just because"; DrawnBy=Maël & PéPé; Revision=Rev 1; Scale=Scale; Sheet=Page 1 de 1
  Height = 215.9
  Orientation = 1
  Width = 279.4
FEATURE [TechDraw::DrawViewPart] View001
  CoarseView = false
  Direction = (0.207,0.686,-0.698)
  Focus = 100
  HardHidden = false
  IsoCount = 0
  IsoHidden = false
  IsoVisible = false
  LockPosition = false
  Perspective = false
  Rotation = 0
  Scale = 0.7
  ScaleType = 0
  SeamHidden = false
  SeamVisible = true
  SmoothHidden = false
  SmoothVisible = true
  Source = -> [Body,Body001,Body010]
  X = 146.884
  XDirection = (-0.176,0.728,0.663)
  XSource = -> [LinkGroup,LinkGroup001]
  Y = 131.376
FEATURE [TechDraw::DrawPage] Page
  KeepUpdated = true
  NextBalloonIndex = 1
  ProjectionType = 0
  Template = -> Template
  Views = -> [View001]
FEATURE [Sketcher::SketchObject] Sketch016
  FullyConstrained = true
  MapMode = 5
  Support = -> [XY_Plane011]
  sketch-geometry (8):
    g0: ArcOfCircle CenterX=0 CenterY=-2.3e-15 CenterZ=0 NormalX=0 NormalY=0 NormalZ=1 AngleXU=0 Radius=23.8 StartAngle=2.2259 EndAngle=4.05728
    g1: ArcOfCircle CenterX=0 CenterY=-2.3e-15 CenterZ=0 NormalX=0 NormalY=0 NormalZ=1 AngleXU=0 Radius=23.8 StartAngle=5.3675 EndAngle=7.19888
    g2: LineSegment StartX=-14.5 StartY=-18.873 StartZ=0 EndX=14.5 EndY=-18.873 EndZ=0
    g3: LineSegment StartX=-14.5 StartY=18.873 StartZ=0 EndX=14.5 EndY=18.873 EndZ=0
    g4: ArcOfCircle CenterX=0 CenterY=-2.3e-15 CenterZ=0 NormalX=0 NormalY=0 NormalZ=1 AngleXU=0 Radius=22.6 StartAngle=2.22941 EndAngle=4.05377
    g5: ArcOfCircle CenterX=0 CenterY=-2.3e-15 CenterZ=0 NormalX=0 NormalY=0 NormalZ=1 AngleXU=0 Radius=22.6 StartAngle=5.371 EndAngle=7.19537
    g6: LineSegment StartX=-13.8317 StartY=17.873 StartZ=0 EndX=13.8317 EndY=17.873 EndZ=0
    g7: LineSegment StartX=13.8317 StartY=-17.873 StartZ=0 EndX=-13.8317 EndY=-17.873 EndZ=0
  constraints (22):
    c: Coincident(g0,g-1)
    c: Coincident(g0,g1)
    c: Coincident(g0,g2)
    c: Coincident(g1,g2)
    c: Coincident(g1,g3)
    c: Coincident(g0,g3)
    c: Symmetric(g1,g0,g-2)
    c: Symmetric(g0,g1,g-2)
    c: Radius(g1) = 23.8
    c: Symmetric(g0,g0,g-1)
    c: DistanceX(g2,g2) = 29
    c: Coincident(g4,g0)
    c: Coincident(g5,g0)
    c: Coincident(g6,g4)
    c: Coincident(g6,g5)
    c: Coincident(g7,g5)
    c: Coincident(g7,g4)
    c: Symmetric(g5,g5,g-1)
    c: Symmetric(g5,g4,g-2)
    c: Radius(g5) = 22.6
    c: Horizontal(g7)
    c: Distance(g4,g3) = 1
FEATURE [PartDesign::Pad] Pad010
  Direction = (1,1,1)
  Length = 10
  Length2 = 100
  Profile = -> Sketch016
  Type = 0
FEATURE [PartDesign::Chamfer] Chamfer003
  Angle = 45
  Base = -> Pad010 [Edge7,Edge12]
  BaseFeature = -> Pad010
  ChamferType = 0
  FlipDirection = false
  Size = 0.5
  Size2 = 1
  SupportTransform = false
FEATURE [Sketcher::SketchObject] Sketch017
  FullyConstrained = true
  MapMode = 5
  Placement = pos=(0,0,0) rot=(1,0,0;3.14159rad)
  Support = -> [Chamfer003]
  sketch-geometry (2):
    g0: Circle CenterX=0 CenterY=0 CenterZ=0 NormalX=0 NormalY=0 NormalZ=1 AngleXU=0 Radius=23.9
    g1: Circle CenterX=0 CenterY=0 CenterZ=0 NormalX=0 NormalY=0 NormalZ=1 AngleXU=0 Radius=22.6
  constraints (4):
    c: Coincident(g0,g-1)
    c: Radius(g0) = 23.9
    c: Coincident(g1,g0)
    c: Radius(g1) = 22.6
FEATURE [PartDesign::Pad] Pad011
  BaseFeature = -> Chamfer003
  Direction = (1,1,1)
  Length = 20
  Length2 = 100
  Profile = -> Sketch017
  Type = 0
FEATURE [Sketcher::SketchObject] Sketch018
  ExternalGeometry = -> [Pad011]
  FullyConstrained = true
  MapMode = 5
  Placement = pos=(0,0,0) rot=(1,0,0;3.14159rad)
  Support = -> [Pad011]
  sketch-geometry (4):
    g0: ArcOfCircle CenterX=-1.1e-15 CenterY=0 CenterZ=0 NormalX=0 NormalY=0 NormalZ=1 AngleXU=0 Radius=23.9 StartAngle=3.98637 EndAngle=5.43841
    g1: ArcOfCircle CenterX=-1.1e-15 CenterY=0 CenterZ=0 NormalX=0 NormalY=0 NormalZ=1 AngleXU=0 Radius=23.9 StartAngle=0.844779 EndAngle=2.29681
    g2: LineSegment StartX=-15.8671 StartY=17.873 StartZ=0 EndX=15.8671 EndY=17.873 EndZ=0
    g3: LineSegment StartX=-15.8671 StartY=-17.873 StartZ=0 EndX=15.8671 EndY=-17.873 EndZ=0
  constraints (14):
    c: Coincident(g0,g-1)
    c: PointOnObject(g0,g-3)
    c: PointOnObject(g0,g-3)
    c: Coincident(g1,g0)
    c: PointOnObject(g1,g-3)
    c: PointOnObject(g1,g-3)
    c: Coincident(g2,g1)
    c: Coincident(g2,g1)
    c: Horizontal(g2)
    c: PointOnObject(g-4,g2)
    c: Coincident(g3,g0)
    c: Coincident(g3,g0)
    c: Horizontal(g3)
    c: PointOnObject(g-5,g3)
FEATURE [PartDesign::Pad] Pad012
  BaseFeature = -> Pad011
  Direction = (1,1,1)
  Length = 2
  Length2 = 100
  Profile = -> Sketch018
  Type = 0
FEATURE [Sketcher::SketchObject] Sketch019
  ExternalGeometry = -> [Pad012]
  FullyConstrained = true
  MapMode = 5
  Placement = pos=(0,0,-20) rot=(1,0,0;3.14159rad)
  Support = -> [Pad012]
  sketch-geometry (3):
    g0: Circle CenterX=-18 CenterY=4 CenterZ=0 NormalX=0 NormalY=0 NormalZ=1 AngleXU=0 Radius=1.5
    g1: Circle CenterX=-18 CenterY=-4 CenterZ=0 NormalX=0 NormalY=0 NormalZ=1 AngleXU=0 Radius=1.5
    g2: Circle CenterX=0 CenterY=0 CenterZ=0 NormalX=0 NormalY=0 NormalZ=1 AngleXU=0 Radius=23.9
  constraints (7):
    c: Radius(g1) = 1.5
    c: Equal(g1,g0)
    c: Symmetric(g0,g1,g-1)
    c: DistanceX(g0) = -18
    c: DistanceY(g0) = 4
    c: Radius(g2) = 23.9
    c: Coincident(g2,g-1)
FEATURE [PartDesign::Pad] Pad013
  BaseFeature = -> Pad012
  Direction = (1,1,1)
  Length = 2
  Length2 = 100
  Profile = -> Sketch019
  Type = 0
FEATURE [PartDesign::Chamfer] Chamfer004
  Angle = 45
  Base = -> Pad013 [Edge42]
  BaseFeature = -> Pad013
  ChamferType = 0
  FlipDirection = false
  Size = 1
  Size2 = 1
  SupportTransform = false
FEATURE [PartDesign::Body] Body011  label="couvercle_coiffe_V1"
  Group = -> [Sketch016,Pad010,Chamfer003,Sketch017,Pad011,Sketch018,Pad012,Sketch019,Pad013,Chamfer004]
  Origin = -> Origin011
  Placement = pos=(0,0,200.3) rot=(0,0,1;0rad)
  Tip = -> Chamfer004
FEATURE [Mesh::Feature] Mesh001  label="couvercle_coiffe_V1 (Meshed)"
FEATURE [Sketcher::SketchObject] Sketch020
  FullyConstrained = true
  MapMode = 5
  Support = -> [XY_Plane012]
  sketch-geometry (2):
    g0: Circle CenterX=0 CenterY=0 CenterZ=0 NormalX=0 NormalY=0 NormalZ=1 AngleXU=0 Radius=9.25
    g1: Circle CenterX=0 CenterY=0 CenterZ=0 NormalX=0 NormalY=0 NormalZ=1 AngleXU=0 Radius=11.75
  constraints (4):
    c: Coincident(g0,g-1)
    c: Coincident(g1,g0)
    c: Radius(g1) = 11.75
    c: Radius(g0) = 9.25
FEATURE [PartDesign::Pad] Pad014
  Direction = (1,1,1)
  Length = 70
  Length2 = 100
  Profile = -> Sketch020
  Type = 0
FEATURE [Sketcher::SketchObject] Sketch021
  FullyConstrained = true
  MapMode = 5
  Placement = pos=(0,0,0) rot=(1,0,0;3.14159rad)
  Support = -> [Pad014]
  sketch-geometry (4):
    g0: LineSegment StartX=-15.74 StartY=1.5 StartZ=0 EndX=15.74 EndY=1.5 EndZ=0
    g1: LineSegment StartX=15.74 StartY=1.5 StartZ=0 EndX=15.74 EndY=-1.5 EndZ=0
    g2: LineSegment StartX=15.74 StartY=-1.5 StartZ=0 EndX=-15.74 EndY=-1.5 EndZ=0
    g3: LineSegment StartX=-15.74 StartY=-1.5 StartZ=0 EndX=-15.74 EndY=1.5 EndZ=0
  constraints (11):
    c: Coincident(g0,g1)
    c: Coincident(g1,g2)
    c: Coincident(g2,g3)
    c: Coincident(g3,g0)
    c: Horizontal(g0)
    c: Horizontal(g2)
    c: Vertical(g1)
    c: Vertical(g3)
    c: Symmetric(g1,g0,g-1)
    c: DistanceX(g2,g2) = 31.48
    c: DistanceY(g1,g1) = 3
FEATURE [PartDesign::Pocket] Pocket004
  BaseFeature = -> Pad014
  Length = 67
  Length2 = 100
  Profile = -> Sketch021
  Type = 0
FEATURE [PartDesign::Chamfer] Chamfer005
  Angle = 45
  Base = -> Pocket004 [Edge3,Edge7]
  BaseFeature = -> Pocket004
  ChamferType = 0
  FlipDirection = false
  Size = 2
  Size2 = 1
  SupportTransform = false
FEATURE [Sketcher::SketchObject] Sketch022
  FullyConstrained = true
  MapMode = 5
  Placement = pos=(0,0,0) rot=(1,0,0;3.14159rad)
  Support = -> [Chamfer005]
  sketch-geometry (4):
    g0: LineSegment StartX=-1.5 StartY=15.795 StartZ=0 EndX=1.5 EndY=15.795 EndZ=0
    g1: LineSegment StartX=1.5 StartY=15.795 StartZ=0 EndX=1.5 EndY=-15.795 EndZ=0
    g2: LineSegment StartX=1.5 StartY=-15.795 StartZ=0 EndX=-1.5 EndY=-15.795 EndZ=0
    g3: LineSegment StartX=-1.5 StartY=-15.795 StartZ=0 EndX=-1.5 EndY=15.795 EndZ=0
  constraints (11):
    c: Coincident(g0,g1)
    c: Coincident(g1,g2)
    c: Coincident(g2,g3)
    c: Coincident(g3,g0)
    c: Horizontal(g0)
    c: Horizontal(g2)
    c: Vertical(g1)
    c: Vertical(g3)
    c: Symmetric(g1,g0,g-1)
    c: DistanceX(g2,g2) = 3
    c: DistanceY(g1,g1) = 31.59
FEATURE [PartDesign::Pocket] Pocket005
  BaseFeature = -> Chamfer005
  Length = 67
  Length2 = 100
  Profile = -> Sketch022
  Type = 0
FEATURE [PartDesign::Body] Body012  label="Adaptateur_moteur_V1"
  Group = -> [Sketch020,Pad014,Sketch021,Pocket004,Chamfer005,Sketch022,Pocket005]
  Origin = -> Origin012
  Placement = pos=(0,8e-15,69) rot=(1,0,0;3.14159rad)
  Tip = -> Pocket005
FEATURE [Mesh::Feature] Mesh002  label="couvercle_coiffe_V1 (Meshed)001"
FEATURE [Sketcher::SketchObject] Sketch023
  FullyConstrained = true
  MapMode = 5
  Support = -> [XY_Plane013]
  sketch-geometry (2):
    g0: Circle CenterX=0 CenterY=0 CenterZ=0 NormalX=0 NormalY=0 NormalZ=1 AngleXU=0 Radius=9.25
    g1: Circle CenterX=0 CenterY=0 CenterZ=0 NormalX=0 NormalY=0 NormalZ=1 AngleXU=0 Radius=11.75
  constraints (4):
    c: Coincident(g0,g-1)
    c: Coincident(g1,g0)
    c: Radius(g1) = 11.75
    c: Radius(g0) = 9.25
FEATURE [PartDesign::Pad] Pad015
  Direction = (1,1,1)
  Length = 70
  Length2 = 100
  Profile = -> Sketch023
  Type = 0
FEATURE [Sketcher::SketchObject] Sketch025
  FullyConstrained = true
  MapMode = 5
  Placement = pos=(0,0,0) rot=(1,0,0;3.14159rad)
  Support = -> [Pad015]
  sketch-geometry (4):
    g0: LineSegment StartX=-15.74 StartY=1.5 StartZ=0 EndX=15.74 EndY=1.5 EndZ=0
    g1: LineSegment StartX=15.74 StartY=1.5 StartZ=0 EndX=15.74 EndY=-1.5 EndZ=0
    g2: LineSegment StartX=15.74 StartY=-1.5 StartZ=0 EndX=-15.74 EndY=-1.5 EndZ=0
    g3: LineSegment StartX=-15.74 StartY=-1.5 StartZ=0 EndX=-15.74 EndY=1.5 EndZ=0
  constraints (11):
    c: Coincident(g0,g1)
    c: Coincident(g1,g2)
    c: Coincident(g2,g3)
    c: Coincident(g3,g0)
    c: Horizontal(g0)
    c: Horizontal(g2)
    c: Vertical(g1)
    c: Vertical(g3)
    c: Symmetric(g1,g0,g-1)
    c: DistanceX(g2,g2) = 31.48
    c: DistanceY(g1,g1) = 3
FEATURE [PartDesign::Pocket] Pocket007
  BaseFeature = -> Pad015
  Length = 67
  Length2 = 100
  Profile = -> Sketch025
  Type = 0
FEATURE [PartDesign::Chamfer] Chamfer006
  Angle = 45
  Base = -> Pocket007 [Edge3,Edge7]
  BaseFeature = -> Pocket007
  ChamferType = 0
  FlipDirection = false
  Size = 2
  Size2 = 1
  SupportTransform = false
FEATURE [Sketcher::SketchObject] Sketch024
  ExternalGeometry = -> [Chamfer006]
  FullyConstrained = true
  MapMode = 5
  Placement = pos=(0,0,0) rot=(1,0,0;3.14159rad)
  Support = -> [Chamfer006]
  sketch-geometry (8):
    g0: LineSegment StartX=-1.5 StartY=13.94 StartZ=0 EndX=11.6539 EndY=13.94 EndZ=0
    g1: LineSegment StartX=11.6539 StartY=13.94 StartZ=0 EndX=11.6539 EndY=1.5 EndZ=0
    g2: LineSegment StartX=11.6539 StartY=1.5 StartZ=0 EndX=-1.5 EndY=1.5 EndZ=0
    g3: LineSegment StartX=-1.5 StartY=1.5 StartZ=0 EndX=-1.5 EndY=13.94 EndZ=0
    g4: LineSegment StartX=-11.6539 StartY=-1.5 StartZ=0 EndX=1.5 EndY=-1.5 EndZ=0
    g5: LineSegment StartX=1.5 StartY=-1.5 StartZ=0 EndX=1.5 EndY=-13.94 EndZ=0
    g6: LineSegment StartX=1.5 StartY=-13.94 StartZ=0 EndX=-11.6539 EndY=-13.94 EndZ=0
    g7: LineSegment StartX=-11.6539 StartY=-13.94 StartZ=0 EndX=-11.6539 EndY=-1.5 EndZ=0
  constraints (21):
    c: Coincident(g0,g1)
    c: Coincident(g1,g2)
    c: Coincident(g2,g3)
    c: Coincident(g3,g0)
    c: Horizontal(g0)
    c: Horizontal(g2)
    c: Vertical(g1)
    c: Vertical(g3)
    c: Coincident(g1,g-3)
    c: DistanceX(g-2,g0) = -1.5
    c: DistanceY(g1,g1) = 12.44
    c: Coincident(g4,g5)
    c: Coincident(g5,g6)
    c: Coincident(g6,g7)
    c: Coincident(g7,g4)
    c: Horizontal(g4)
    c: Horizontal(g6)
    c: Vertical(g5)
    c: Vertical(g7)
    c: Coincident(g4,g-4)
    c: Symmetric(g5,g0,g-1)
FEATURE [PartDesign::Pocket] Pocket006
  BaseFeature = -> Chamfer006
  Length = 67
  Length2 = 100
  Profile = -> Sketch024
  Type = 0
FEATURE [PartDesign::Body] Body013  label="Adaptateur_moteur_V2"
  Group = -> [Sketch023,Pad015,Sketch025,Pocket007,Chamfer006,Sketch024,Pocket006]
  Origin = -> Origin013
  Placement = pos=(0,8e-15,69) rot=(1,0,0;3.14159rad)
  Tip = -> Pocket006
